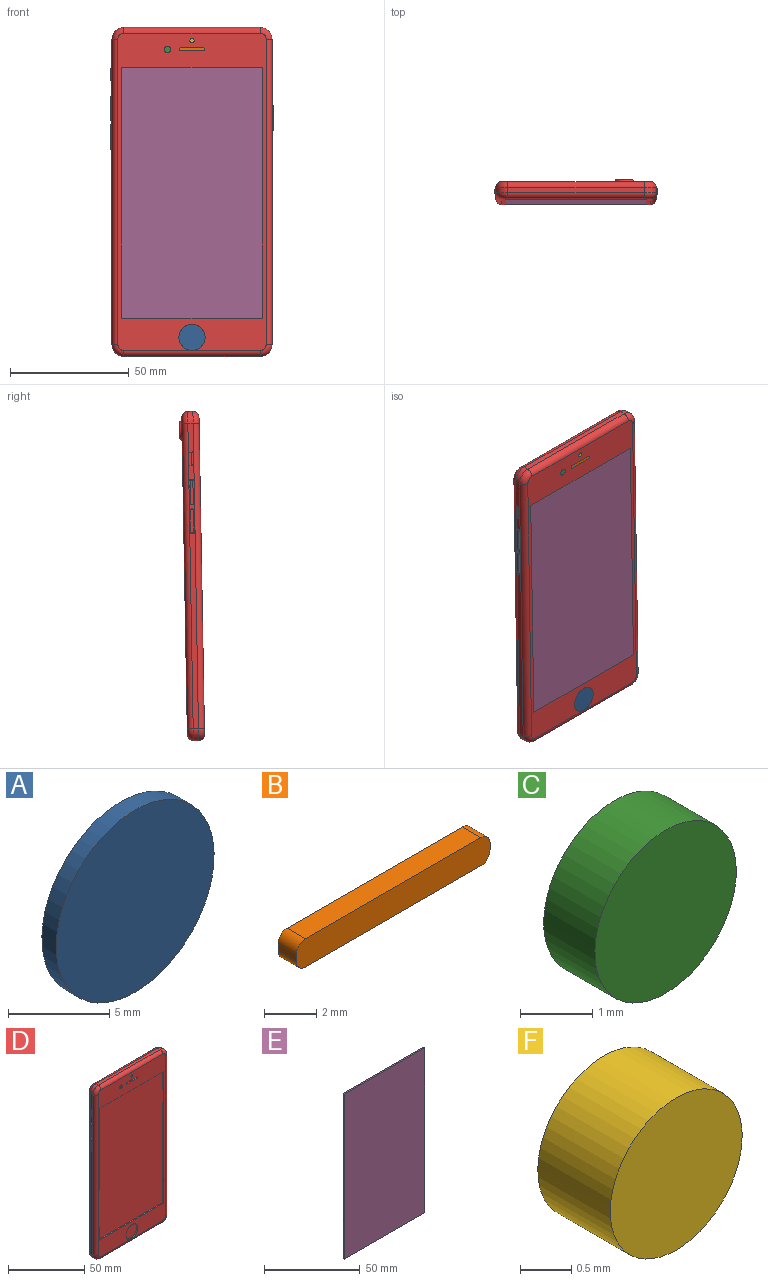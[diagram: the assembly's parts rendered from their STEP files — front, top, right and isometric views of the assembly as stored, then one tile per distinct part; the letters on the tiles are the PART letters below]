
ASSEMBLY  parts=6 mates=5
PART A: 3 faces, bbox 11x1x11 mm
  f0: cylinder r=5.52mm len=11.04mm, axis (0,1,0), area 34.7mm2, adj f1,f2
  f1: plane 11.04x11.04mm, normal (0,-1,0), area 95.7mm2, adj f0
  f2: plane 11.04x11.04mm, normal (0,1,0), area 95.7mm2, adj f0
PART B: 10 faces, bbox 10.5x1x1.3 mm
  f0: plane 9.53x1mm, normal (0,0,1), area 9.5mm2, adj f1,f7,f8,f9
  f1: cylinder r=0.5mm len=1mm, axis (0,1,0), area 0.8mm2, adj f0,f2,f8,f9
  f2: plane 1x0.33mm, normal (-1,0,0), area 0.3mm2, adj f1,f3,f8,f9
  f3: cylinder r=0.5mm len=1mm, axis (0,1,0), area 0.8mm2, adj f2,f4,f8,f9
  f4: plane 9.53x1mm, normal (0,0,-1), area 9.5mm2, adj f3,f5,f8,f9
  f5: cylinder r=0.5mm len=1mm, axis (0,1,0), area 0.8mm2, adj f4,f6,f8,f9
  f6: plane 1x0.33mm, normal (1,0,0), area 0.3mm2, adj f5,f7,f8,f9
  f7: cylinder r=0.5mm len=1mm, axis (0,1,0), area 0.8mm2, adj f0,f6,f8,f9
  f8: plane 10.53x1.33mm, normal (0,-1,0), area 13.8mm2, adj f0,f1,f2,f3,f4,f5,f6,f7
  f9: plane 10.53x1.33mm, normal (0,1,0), area 13.8mm2, adj f0,f1,f2,f3,f4,f5,f6,f7
PART C: 3 faces, bbox 2.8x1x2.8 mm
  f0: cylinder r=1.38mm len=2.76mm, axis (0,1,0), area 8.7mm2, adj f1,f2
  f1: plane 2.76x2.76mm, normal (0,-1,0), area 6mm2, adj f0
  f2: plane 2.76x2.76mm, normal (0,1,0), area 6mm2, adj f0
PART D: 148 faces, bbox 68.3x8.9x139.1 mm
  f0: cylinder r=2.89mm len=5.78mm, axis (0,-1,0), area 1.8mm2, adj f141,f147
  f1: plane 47.27x2.22mm, normal (0,0,-1), area 77.5mm2, adj f6,f93,f101,f116,f118,f119,f120,f121
  f2: plane 133.32x62.28mm, normal (0,1,0), area 8103.5mm2, adj f94,f95,f96,f97,f98,f99,f100,f101
  f3: plane 128.32x2.22mm, normal (-1,0,0), area 223.8mm2, adj f4,f10,f55,f56,f57,f58,f59,f60
  f4: cylinder r=5mm len=5mm, axis (0,-1,0), area 17.4mm2, adj f3,f5,f91,f99
  f5: plane 7.47x2.22mm, normal (0,0,-1), area 15.9mm2, adj f4,f93,f101,f116
  f6: cylinder r=5mm len=5mm, axis (0,-1,0), area 17.4mm2, adj f1,f7,f92,f100
  f7: plane 128.32x2.22mm, normal (1,0,0), area 262.5mm2, adj f6,f8,f32,f33,f34,f35,f36,f37
  f8: cylinder r=5mm len=5mm, axis (0,-1,0), area 17.4mm2, adj f7,f9,f88,f96
  f9: plane 57.28x2.22mm, normal (0,0,1), area 127.2mm2, adj f8,f10,f86,f94
  f10: cylinder r=5mm len=5mm, axis (0,-1,0), area 17.4mm2, adj f3,f9,f87,f95
  f11: plane 133.32x62.28mm, normal (0,-1,0), area 1940.5mm2, adj f12,f13,f14,f15,f17,f19,f21,f22
  f12: plane 59.19x1mm, normal (0,0,1), area 59.2mm2, adj f11,f13,f15,f16
  f13: plane 105.41x1mm, normal (-1,0,0), area 105.4mm2, adj f11,f12,f14,f16
  f14: plane 59.19x1mm, normal (0,0,-1), area 59.2mm2, adj f11,f13,f15,f16
  f15: plane 105.41x1mm, normal (1,0,0), area 105.4mm2, adj f11,f12,f14,f16
  f16: plane 105.41x59.19mm, normal (0,-1,0), area 6239.2mm2, adj f12,f13,f14,f15
  f17: cylinder r=5.52mm len=11.04mm, axis (0,-1,0), area 34.7mm2, adj f11,f18
  f18: plane 11.04x11.04mm, normal (0,-1,0), area 95.7mm2, adj f17
  f19: cylinder r=0.91mm len=1.82mm, axis (0,-1,0), area 5.7mm2, adj f11,f20
  f20: plane 1.82x1.82mm, normal (0,-1,0), area 2.6mm2, adj f19
  f21: plane 1x0.33mm, normal (1,0,0), area 0.3mm2, adj f11,f22,f28,f29
  f22: cylinder r=0.5mm len=1mm, axis (0,-1,0), area 0.8mm2, adj f11,f21,f23,f29
  f23: plane 9.53x1mm, normal (0,0,1), area 9.5mm2, adj f11,f22,f24,f29
  f24: cylinder r=0.5mm len=1mm, axis (0,-1,0), area 0.8mm2, adj f11,f23,f25,f29
  f25: plane 1x0.33mm, normal (-1,0,0), area 0.3mm2, adj f11,f24,f26,f29
  f26: cylinder r=0.5mm len=1mm, axis (0,-1,0), area 0.8mm2, adj f11,f25,f27,f29
  f27: plane 9.53x1mm, normal (0,0,-1), area 9.5mm2, adj f11,f26,f28,f29
  f28: cylinder r=0.5mm len=1mm, axis (0,-1,0), area 0.8mm2, adj f11,f21,f27,f29
  f29: plane 10.53x1.33mm, normal (0,-1,0), area 13.8mm2, adj f21,f22,f23,f24,f25,f26,f27,f28
  f30: cylinder r=1.38mm len=2.76mm, axis (0,-1,0), area 8.7mm2, adj f11,f31
  f31: plane 2.76x2.76mm, normal (0,-1,0), area 6mm2, adj f30
  f32: plane 0.5x0.17mm, normal (0,0,1), area 0.1mm2, adj f7,f33,f39,f40
  f33: cylinder r=1mm len=1mm, axis (-1,0,0), area 0.8mm2, adj f7,f32,f34,f40
  f34: plane 8.71x0.5mm, normal (0,-1,0), area 4.4mm2, adj f7,f33,f35,f40
  f35: cylinder r=1mm len=1mm, axis (-1,0,0), area 0.8mm2, adj f7,f34,f36,f40
  f36: plane 0.5x0.17mm, normal (0,0,-1), area 0.1mm2, adj f7,f35,f37,f40
  f37: cylinder r=1mm len=1mm, axis (-1,0,0), area 0.8mm2, adj f7,f36,f38,f40
  f38: plane 8.71x0.5mm, normal (0,1,0), area 4.4mm2, adj f7,f37,f39,f40
  f39: cylinder r=1mm len=1mm, axis (-1,0,0), area 0.8mm2, adj f7,f32,f38,f40
  f40: plane 10.71x2.17mm, normal (1,0,0), area 22.4mm2, adj f32,f33,f34,f35,f36,f37,f38,f39
  f41: cylinder r=0.4mm len=1.5mm, axis (-1,0,0), area 0.9mm2, adj f42,f64,f65,f84
  f42: plane 1.5x0.37mm, normal (0,0,-1), area 0.6mm2, adj f41,f43,f65,f84
  f43: cylinder r=0.4mm len=1.5mm, axis (-1,0,0), area 0.9mm2, adj f42,f44,f65,f84
  f44: plane 9.31x1.5mm, normal (0,1,0), area 14mm2, adj f43,f45,f65,f84
  f45: cylinder r=0.4mm len=1.5mm, axis (-1,0,0), area 0.9mm2, adj f44,f46,f65,f84
  f46: plane 1.5x0.37mm, normal (0,0,1), area 0.6mm2, adj f45,f47,f65,f84
  f47: cylinder r=0.4mm len=1.5mm, axis (-1,0,0), area 0.9mm2, adj f46,f64,f65,f84
  f48: plane 1.5x0.37mm, normal (0,0,1), area 0.6mm2, adj f49,f62,f65,f85
  f49: cylinder r=0.4mm len=1.5mm, axis (-1,0,0), area 0.9mm2, adj f48,f50,f65,f85
  f50: plane 9.31x1.5mm, normal (0,-1,0), area 14mm2, adj f49,f51,f65,f85
  f51: cylinder r=0.4mm len=1.5mm, axis (-1,0,0), area 0.9mm2, adj f50,f52,f65,f85
  f52: plane 1.5x0.37mm, normal (0,0,-1), area 0.6mm2, adj f51,f53,f65,f85
  f53: cylinder r=0.4mm len=1.5mm, axis (-1,0,0), area 0.9mm2, adj f52,f54,f65,f85
  f54: plane 9.31x1.5mm, normal (0,1,0), area 14mm2, adj f53,f62,f65,f85
  f55: plane 1.17x1mm, normal (0,0,1), area 1.2mm2, adj f3,f56,f63,f65
  f56: cylinder r=0.5mm len=1mm, axis (-1,0,0), area 0.8mm2, adj f3,f55,f57,f65
  f57: plane 21.72x1mm, normal (0,1,0), area 21.7mm2, adj f3,f56,f58,f65
  f58: cylinder r=0.5mm len=1mm, axis (-1,0,0), area 0.8mm2, adj f3,f57,f59,f65
  f59: plane 1.17x1mm, normal (0,0,-1), area 1.2mm2, adj f3,f58,f60,f65
  f60: cylinder r=0.5mm len=1mm, axis (-1,0,0), area 0.8mm2, adj f3,f59,f61,f65
  f61: plane 21.72x1mm, normal (0,-1,0), area 21.7mm2, adj f3,f60,f63,f65
  f62: cylinder r=0.4mm len=1.5mm, axis (-1,0,0), area 0.9mm2, adj f48,f54,f65,f85
  f63: cylinder r=0.5mm len=1mm, axis (-1,0,0), area 0.8mm2, adj f3,f55,f61,f65
  f64: plane 9.31x1.5mm, normal (0,-1,0), area 14mm2, adj f41,f47,f65,f84
  f65: plane 22.72x2.17mm, normal (-1,0,0), area 25.7mm2, adj f41,f42,f43,f44,f45,f46,f47,f48
  f66: cylinder r=0.4mm len=1.5mm, axis (-1,0,0), area 0.9mm2, adj f67,f81,f82,f83
  f67: plane 4.43x1.5mm, normal (0,1,0), area 6.6mm2, adj f66,f68,f82,f83
  f68: cylinder r=0.4mm len=1.5mm, axis (-1,0,0), area 0.9mm2, adj f67,f69,f82,f83
  f69: plane 1.5x0.09mm, normal (0,0,1), area 0.1mm2, adj f68,f70,f82,f83
  f70: cylinder r=0.4mm len=1.5mm, axis (-1,0,0), area 0.9mm2, adj f69,f71,f82,f83
  f71: plane 4.43x1.5mm, normal (0,-1,0), area 6.6mm2, adj f70,f72,f82,f83
  f72: cylinder r=0.4mm len=1.5mm, axis (-1,0,0), area 0.9mm2, adj f71,f81,f82,f83
  f73: plane 1.17x1mm, normal (0,0,1), area 1.2mm2, adj f3,f74,f80,f82
  f74: cylinder r=0.5mm len=1mm, axis (-1,0,0), area 0.8mm2, adj f3,f73,f75,f82
  f75: plane 4.63x1mm, normal (0,1,0), area 4.6mm2, adj f3,f74,f76,f82
  f76: cylinder r=0.5mm len=1mm, axis (-1,0,0), area 0.8mm2, adj f3,f75,f77,f82
  f77: plane 1.17x1mm, normal (0,0,-1), area 1.2mm2, adj f3,f76,f78,f82
  f78: cylinder r=0.5mm len=1mm, axis (-1,0,0), area 0.8mm2, adj f3,f77,f79,f82
  f79: plane 4.63x1mm, normal (0,-1,0), area 4.6mm2, adj f3,f78,f80,f82
  f80: cylinder r=0.5mm len=1mm, axis (-1,0,0), area 0.8mm2, adj f3,f73,f79,f82
  f81: plane 1.5x0.09mm, normal (0,0,-1), area 0.1mm2, adj f66,f72,f82,f83
  f82: plane 5.63x2.17mm, normal (-1,0,0), area 7.5mm2, adj f66,f67,f68,f69,f70,f71,f72,f73
  f83: plane 5.23x0.89mm, normal (-1,0,0), area 4.5mm2, adj f66,f67,f68,f69,f70,f71,f72,f81
  f84: plane 10.11x1.17mm, normal (-1,0,0), area 11.7mm2, adj f41,f42,f43,f44,f45,f46,f47,f64
  f85: plane 10.11x1.17mm, normal (-1,0,0), area 11.7mm2, adj f48,f49,f50,f51,f52,f53,f54,f62
  f86: cylinder r=2.5mm len=57.28mm, axis (-1,0,0), area 224.9mm2, adj f9,f11,f87,f88
  f87: torus R=2.5mm, axis (0,-1,0), area 25.2mm2, adj f10,f11,f86,f89
  f88: torus R=2.5mm, axis (0,-1,0), area 25.2mm2, adj f8,f11,f86,f90
  f89: cylinder r=2.5mm len=128.32mm, axis (0,0,-1), area 503.9mm2, adj f3,f11,f87,f91
  f90: cylinder r=2.5mm len=128.32mm, axis (0,0,1), area 503.9mm2, adj f7,f11,f88,f92
  f91: torus R=2.5mm, axis (0,-1,0), area 25.2mm2, adj f4,f11,f89,f93
  f92: torus R=2.5mm, axis (0,-1,0), area 25.2mm2, adj f6,f11,f90,f93
  f93: cylinder r=2.5mm len=57.28mm, axis (1,0,0), area 223.9mm2, adj f1,f5,f11,f91,f92,f116
  f94: cylinder r=2.5mm len=57.28mm, axis (1,0,0), area 224.9mm2, adj f2,f9,f95,f96
  f95: torus R=2.5mm, axis (0,-1,0), area 25.2mm2, adj f2,f10,f94,f97
  f96: torus R=2.5mm, axis (0,-1,0), area 25.2mm2, adj f2,f8,f94,f98
  f97: cylinder r=2.5mm len=128.32mm, axis (0,0,1), area 503.9mm2, adj f2,f3,f95,f99
  f98: cylinder r=2.5mm len=128.32mm, axis (0,0,-1), area 503.9mm2, adj f2,f7,f96,f100
  f99: torus R=2.5mm, axis (0,-1,0), area 25.2mm2, adj f2,f4,f97,f101
  f100: torus R=2.5mm, axis (0,-1,0), area 25.2mm2, adj f2,f6,f98,f101
  f101: cylinder r=2.5mm len=57.28mm, axis (-1,0,0), area 223.9mm2, adj f1,f2,f5,f99,f100,f116
  f102: cylinder r=2.68mm len=2.63mm, axis (0,1,0), area 0mm2, adj f2,f103,f104
  f103: cylinder r=2.92mm len=2.63mm, axis (0,1,0), area 0mm2, adj f2,f102,f104
  f104: plane 2.63x2.63mm, normal (0,1,0), area 3.6mm2, adj f102,f103
  f105: cylinder r=6.62mm len=9.71mm, axis (0,1,0), area 0.1mm2, adj f2,f106,f114,f115
  f106: cylinder r=1.81mm len=1.97mm, axis (0,1,0), area 0mm2, adj f2,f105,f107,f115
  f107: cylinder r=4.1mm len=4mm, axis (0,1,0), area 0mm2, adj f2,f106,f108,f115
  f108: cylinder r=1.81mm len=1.97mm, axis (0,1,0), area 0mm2, adj f2,f107,f109,f115
  f109: cylinder r=6.62mm len=3.5mm, axis (0,1,0), area 0mm2, adj f2,f108,f110,f115
  f110: cylinder r=2.72mm len=5.27mm, axis (0,1,0), area 0.1mm2, adj f2,f109,f111,f115
  f111: cylinder r=6.62mm len=0.93mm, axis (0,1,0), area 0mm2, adj f2,f110,f112,f115
  f112: cylinder r=2.47mm len=2.94mm, axis (0,1,0), area 0mm2, adj f2,f111,f113,f115
  f113: cylinder r=4.5mm len=4mm, axis (0,1,0), area 0mm2, adj f2,f112,f114,f115
  f114: cylinder r=2.47mm len=2.94mm, axis (0,1,0), area 0mm2, adj f2,f105,f113,f115
  f115: plane 12.99x10.89mm, normal (0,1,0), area 109.7mm2, adj f105,f106,f107,f108,f109,f110,f111,f112
  f116: cylinder r=1.69mm len=9mm, axis (0,0,-1), area 95.4mm2, adj f1,f5,f93,f101,f117
  f117: plane 3.38x3.38mm, normal (0,0,-1), area 9mm2, adj f116
  f118: plane 9x0.2mm, normal (-1,0,0), area 1.8mm2, adj f1,f119,f125,f126
  f119: cylinder r=0.8mm len=9mm, axis (0,0,-1), area 11.3mm2, adj f1,f118,f120,f126
  f120: plane 9x5.78mm, normal (0,1,0), area 52mm2, adj f1,f119,f121,f126
  f121: cylinder r=0.8mm len=9mm, axis (0,0,-1), area 11.3mm2, adj f1,f120,f122,f126
  f122: plane 9x0.2mm, normal (1,0,0), area 1.8mm2, adj f1,f121,f123,f126
  f123: cylinder r=0.8mm len=9mm, axis (0,0,-1), area 11.3mm2, adj f1,f122,f124,f126
  f124: plane 9x5.78mm, normal (0,-1,0), area 52mm2, adj f1,f123,f125,f126
  f125: cylinder r=0.8mm len=9mm, axis (0,0,-1), area 11.3mm2, adj f1,f118,f124,f126
  f126: plane 7.38x1.8mm, normal (0,0,-1), area 12.7mm2, adj f118,f119,f120,f121,f122,f123,f124,f125
  f127: cylinder r=0.8mm len=1.6mm, axis (0,0,-1), area 5mm2, adj f1,f128
  f128: plane 1.6x1.6mm, normal (0,0,-1), area 2mm2, adj f127
  f129: cylinder r=0.8mm len=1.6mm, axis (0,0,-1), area 5mm2, adj f1,f130
  f130: plane 1.6x1.6mm, normal (0,0,-1), area 2mm2, adj f129
  f131: cylinder r=0.8mm len=1.6mm, axis (0,0,-1), area 5mm2, adj f1,f132
  f132: plane 1.6x1.6mm, normal (0,0,-1), area 2mm2, adj f131
  f133: cylinder r=0.8mm len=1.6mm, axis (0,0,-1), area 5mm2, adj f1,f134
  f134: plane 1.6x1.6mm, normal (0,0,-1), area 2mm2, adj f133
  f135: cylinder r=0.8mm len=1.6mm, axis (0,0,-1), area 5mm2, adj f1,f136
  f136: plane 1.6x1.6mm, normal (0,0,-1), area 2mm2, adj f135
  f137: cylinder r=0.8mm len=1.6mm, axis (0,0,-1), area 5mm2, adj f1,f138
  f138: plane 1.6x1.6mm, normal (0,0,-1), area 2mm2, adj f137
  f139: cylinder r=0.8mm len=1.6mm, axis (0,0,-1), area 5mm2, adj f1,f140
  f140: plane 1.6x1.6mm, normal (0,0,-1), area 2mm2, adj f139
  f141: plane 7.23x7.23mm, normal (0,1,0), area 14.8mm2, adj f0,f146
  f142: cylinder r=1.98mm len=3.96mm, axis (0,1,0), area 6.2mm2, adj f2,f143
  f143: plane 3.96x3.96mm, normal (0,1,0), area 12.3mm2, adj f142
  f144: cylinder r=0.74mm len=1.49mm, axis (0,1,0), area 2.3mm2, adj f2,f145
  f145: plane 1.49x1.49mm, normal (0,1,0), area 1.7mm2, adj f144
  f146: torus R=4.62mm, axis (0,-1,0), area 39.3mm2, adj f2,f141
  f147: plane 5.78x5.78mm, normal (0,1,0), area 26.2mm2, adj f0
PART E: 6 faces, bbox 59.2x1x105.4 mm
  f0: plane 59.19x1mm, normal (0,0,1), area 59.2mm2, adj f1,f3,f4,f5
  f1: plane 105.41x1mm, normal (-1,0,0), area 105.4mm2, adj f0,f2,f4,f5
  f2: plane 59.19x1mm, normal (0,0,-1), area 59.2mm2, adj f1,f3,f4,f5
  f3: plane 105.41x1mm, normal (1,0,0), area 105.4mm2, adj f0,f2,f4,f5
  f4: plane 105.41x59.19mm, normal (0,-1,0), area 6239.2mm2, adj f0,f1,f2,f3
  f5: plane 105.41x59.19mm, normal (0,1,0), area 6239.2mm2, adj f0,f1,f2,f3
PART F: 3 faces, bbox 1.8x1x1.8 mm
  f0: cylinder r=0.91mm len=1.82mm, axis (0,1,0), area 5.7mm2, adj f1,f2
  f1: plane 1.82x1.82mm, normal (0,-1,0), area 2.6mm2, adj f0
  f2: plane 1.82x1.82mm, normal (0,1,0), area 2.6mm2, adj f0
PLACE A rot(axis=(1,0,0),179deg) t=(148.33,-5.16,-95.8)mm
PLACE B rot(axis=(0,0.01,1),180deg) t=(-149.1,-3.62,-7.9)mm
PLACE C rot(axis=(-1,0,0),1deg) t=(148.33,-2.62,-7.92)mm
PLACE D rot(axis=(-1,0,0),1deg) t=(-0.39,-3.32,9.28)mm
PLACE E rot(axis=(1,0,0),179deg) t=(148.33,-3.04,25.63)mm
PLACE F rot(axis=(-1,0,0),1deg) t=(148.33,-2.62,-7.92)mm
MATE fastened E.f4 <-> D.f16  axis (0,1,-0.02) through (-0.39,-2.33,8.85)mm
MATE fastened C.f0 <-> D.f30  axis (0,-1,0.02) through (-10.63,-2.28,69.14)mm
MATE fastened B.f8 <-> D.f29  axis (0,1,-0.02) through (-0.39,-1.29,68.45)mm
MATE fastened F.f0 <-> D.f19  axis (0,-1,0.02) through (-0.39,-2.21,72.81)mm
MATE fastened A.f0 <-> D.f17  axis (0,1,-0.02) through (-0.39,-3.39,-51.87)mm
